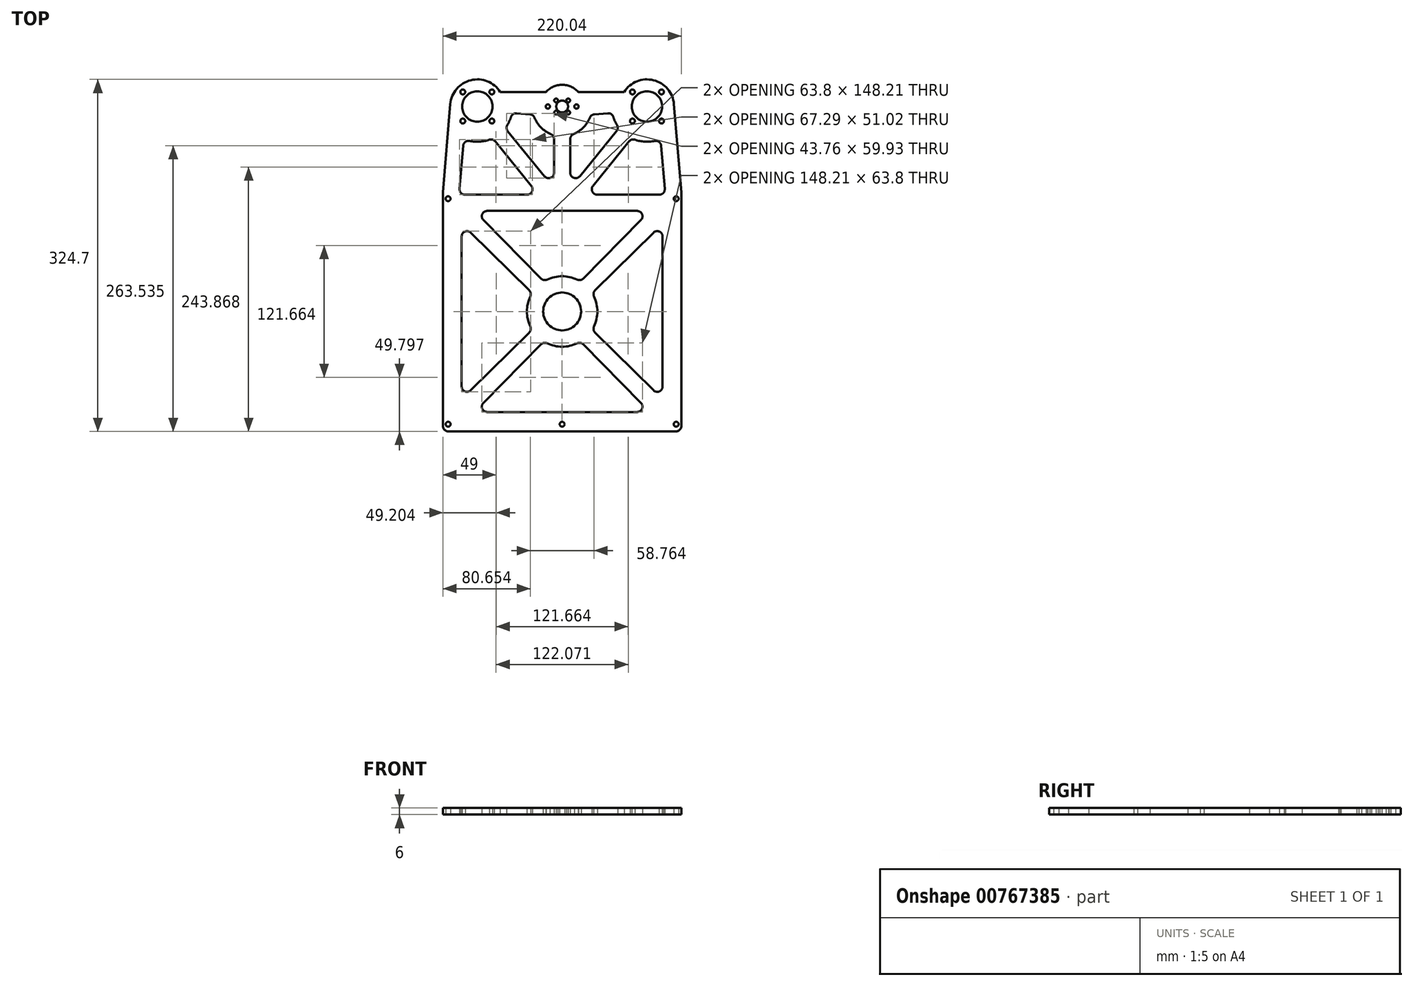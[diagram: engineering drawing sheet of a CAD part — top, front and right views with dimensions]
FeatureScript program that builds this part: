
annotation { "Feature Type Name" : "Feature", "Feature Type Description" : "" }
export const myFeature = defineFeature(function(context is Context, id is Id, definition is map)
    precondition{}
    {
        {
            var Q0;
            Q0=qCreatedBy(makeId("Top.planeOp"),FACE);
            var sketch = newSketch(context, id + "F0", { "sketchPlane" : qUnion([Q0])});
            skLineSegment(sketch, "E0.bottom", {"start": v(129, 146.19) * mm, "end": v(132, 146.19) * mm});
            skLineSegment(sketch, "E1", {"start": v(121.23, -173.81) * mm, "end": v(121.23, 96.42) * mm, "construction": true});
            skPoint(sketch, "E1.endSnap0", {"position": v(16, 96.42) * mm});
            skLineSegment(sketch, "E2", {"start": v(-89.23, -173.81) * mm, "end": v(-89.28, 96.42) * mm, "construction": true});
            skLineSegment(sketch, "E3", {"start": v(-89.28, 96.42) * mm, "end": v(-89.28, 103.45) * mm, "construction": true});
            skLineSegment(sketch, "E4", {"start": v(121.23, 96.42) * mm, "end": v(121.23, 146.19) * mm, "construction": true});
            skCircle(sketch, "E5", {"center": v(-89.27, 41.19) * mm, "radius": 2.25 * mm});
            skCircle(sketch, "E6", {"center": v(-89.23, -166.81) * mm, "radius": 2.25 * mm});
            skCircle(sketch, "E7", {"center": v(121.23, -166.81) * mm, "radius": 2.25 * mm});
            skCircle(sketch, "E8", {"center": v(121.23, 41.19) * mm, "radius": 2.25 * mm});
            skPoint(sketch, "E9.startSnap0", {"position": v(16, -62.81) * mm});
            skLineSegment(sketch, "E10.bottom", {"start": v(-89.04, -173.44) * mm, "end": v(121, -173.44) * mm});
            skLineSegment(sketch, "E10.top", {"start": v(-94.04, 46.77) * mm, "end": v(126, 46.77) * mm, "construction": true});
            skLineSegment(sketch, "E10.left", {"start": v(-94.04, -168.44) * mm, "end": v(-94.04, 46.35) * mm});
            skLineSegment(sketch, "E10.right", {"start": v(126, -168.44) * mm, "end": v(126, 46.36) * mm});
            skLineSegment(sketch, "E11", {"start": v(-89.23, -166.81) * mm, "end": v(121.23, -166.81) * mm, "construction": true});
            skCircle(sketch, "E12", {"center": v(16, -166.81) * mm, "radius": 2.25 * mm});
            skCircle(sketch, "E13", {"center": v(16, 126.26) * mm, "radius": 5.47 * mm});
            skCircle(sketch, "E14", {"center": v(-62.27, 126.26) * mm, "radius": 19 * mm, "construction": true});
            skCircle(sketch, "E15", {"center": v(94.27, 126.26) * mm, "radius": 19 * mm, "construction": true});
            skCircle(sketch, "E16", {"center": v(-62.27, 126.26) * mm, "radius": 14 * mm});
            skCircle(sketch, "E17", {"center": v(94.27, 126.26) * mm, "radius": 14 * mm});
            skCircle(sketch, "E18", {"center": v(-62.27, 126.26) * mm, "radius": 24 * mm, "construction": true});
            skCircle(sketch, "E19", {"center": v(94.27, 126.26) * mm, "radius": 24 * mm, "construction": true});
            skLineSegment(sketch, "E20", {"start": v(-62.27, 126.26) * mm, "end": v(-44.6, 143.94) * mm, "construction": true});
            skCircle(sketch, "E21", {"center": v(-48.84, 139.7) * mm, "radius": 2.25 * mm});
            skCircle(sketch, "E22", {"center": v(-48.84, 139.7) * mm, "radius": 4.25 * mm, "construction": true});
            skCircle(sketch, "E23.1.0", {"center": v(-75.7, 139.7) * mm, "radius": 2.25 * mm});
            skCircle(sketch, "E23.1.1", {"center": v(-75.7, 139.7) * mm, "radius": 4.25 * mm, "construction": true});
            skCircle(sketch, "E23.2.0", {"center": v(-75.7, 112.83) * mm, "radius": 2.25 * mm});
            skCircle(sketch, "E23.2.1", {"center": v(-75.7, 112.83) * mm, "radius": 4.25 * mm, "construction": true});
            skCircle(sketch, "E23.3.0", {"center": v(-48.84, 112.83) * mm, "radius": 2.25 * mm});
            skCircle(sketch, "E23.3.1", {"center": v(-48.84, 112.83) * mm, "radius": 4.25 * mm, "construction": true});
            skLineSegment(sketch, "E24", {"start": v(94.27, 126.26) * mm, "end": v(138.16, 170.16) * mm, "construction": true});
            skCircle(sketch, "E25", {"center": v(107.7, 139.7) * mm, "radius": 2.25 * mm});
            skCircle(sketch, "E26", {"center": v(107.7, 139.7) * mm, "radius": 4.25 * mm, "construction": true});
            skCircle(sketch, "E27.1.0", {"center": v(80.83, 139.7) * mm, "radius": 2.25 * mm});
            skCircle(sketch, "E27.1.1", {"center": v(80.83, 139.7) * mm, "radius": 4.25 * mm, "construction": true});
            skCircle(sketch, "E27.2.0", {"center": v(80.83, 112.83) * mm, "radius": 2.25 * mm});
            skCircle(sketch, "E27.2.1", {"center": v(80.83, 112.83) * mm, "radius": 4.25 * mm, "construction": true});
            skCircle(sketch, "E27.3.0", {"center": v(107.7, 112.83) * mm, "radius": 2.25 * mm});
            skCircle(sketch, "E27.3.1", {"center": v(107.7, 112.83) * mm, "radius": 4.25 * mm, "construction": true});
            skLineSegment(sketch, "E28", {"start": v(21.47, 126.26) * mm, "end": v(36, 126.26) * mm});
            skLineSegment(sketch, "E29", {"start": v(-23.88, -176.81) * mm, "end": v(-3.88, -176.81) * mm});
            skLineSegment(sketch, "E30", {"start": v(35.87, -176.81) * mm, "end": v(55.87, -176.81) * mm});
            skLineSegment(sketch, "E31", {"start": v(-23.9, 41.19) * mm, "end": v(-112.07, 41.19) * mm, "construction": true});
            skLineSegment(sketch, "E32", {"start": v(55.87, 41.19) * mm, "end": v(139.91, 41.19) * mm, "construction": true});
            skLineSegment(sketch, "E33", {"start": v(194.89, 122.83) * mm, "end": v(194.89, 102.83) * mm});
            skLineSegment(sketch, "E34", {"start": v(194.89, 149.7) * mm, "end": v(194.89, 129.7) * mm});
            skCircle(sketch, "E35", {"center": v(16, 126.26) * mm, "radius": 13.2 * mm, "construction": true});
            skCircle(sketch, "E36", {"center": v(16, 126.26) * mm, "radius": 18.25 * mm, "construction": true});
            skCircle(sketch, "E37", {"center": v(29.2, 126.26) * mm, "radius": 2 * mm});
            skArc(sketch, "E38", {"start": v(-41.2, 139.7) * mm, "mid": v(-68.26, 150.54) * mm, "end": v(-87.19, 128.36) * mm});
            skLineSegment(sketch, "E39", {"start": v(-94, 47.2) * mm, "end": v(-87.19, 128.36) * mm});
            skArc(sketch, "E40", {"start": v(36, 126.26) * mm, "mid": v(23.2, 144.92) * mm, "end": v(1.18, 139.7) * mm});
            skLineSegment(sketch, "E41", {"start": v(-41.2, 139.7) * mm, "end": v(1.18, 139.7) * mm});
            skPoint(sketch, "E42.orphan", {"position": v(-84.23, -166.81) * mm});
            skLineSegment(sketch, "E43", {"start": v(-84.23, -161.87) * mm, "end": v(-84.23, 36.25) * mm, "construction": true});
            skArc(sketch, "E44", {"start": v(-1.79, -45.24) * mm, "mid": v(-9, -62.81) * mm, "end": v(-1.79, -80.38) * mm, "construction": true});
            skLineSegment(sketch, "E45.trimOffspring", {"start": v(-84.23, 36.25) * mm, "end": v(-1.79, -45.24) * mm, "construction": true});
            skLineSegment(sketch, "E46.trimOffspring", {"start": v(119.63, 39.6) * mm, "end": v(121.23, 41.19) * mm, "construction": true});
            skLineSegment(sketch, "E47.trimOffspring", {"start": v(119.63, -165.23) * mm, "end": v(121.23, -166.81) * mm, "construction": true});
            skLineSegment(sketch, "E48.trimOffspring", {"start": v(-84.23, -161.87) * mm, "end": v(-1.79, -80.38) * mm, "construction": true});
            skLineSegment(sketch, "E49.0", {"start": v(-68.22, 9.88) * mm, "end": v(-14.42, -43.3) * mm});
            skLineSegment(sketch, "E49.1", {"start": v(-76.73, -131.94) * mm, "end": v(-76.73, 6.32) * mm});
            skLineSegment(sketch, "E49.2", {"start": v(-68.22, -135.5) * mm, "end": v(-14.42, -82.33) * mm});
            skArc(sketch, "E49.3", {"start": v(-13.41, -48.98) * mm, "mid": v(-16.5, -62.81) * mm, "end": v(-13.41, -76.64) * mm});
            skPoint(sketch, "E50.visualSharp", {"position": v(-76.73, 18.3) * mm});
            skArc(sketch, "E50.filletArc", {"start": v(-68.22, 9.88) * mm, "mid": v(-73.66, 10.93) * mm, "end": v(-76.73, 6.32) * mm});
            skPoint(sketch, "E51.visualSharp", {"position": v(-76.73, -143.91) * mm});
            skArc(sketch, "E51.filletArc", {"start": v(-76.73, -131.94) * mm, "mid": v(-73.66, -136.55) * mm, "end": v(-68.22, -135.5) * mm});
            skPoint(sketch, "E52.visualSharp", {"position": v(-11.77, -79.7) * mm});
            skArc(sketch, "E52.filletArc", {"start": v(-14.42, -82.33) * mm, "mid": v(-13.01, -79.65) * mm, "end": v(-13.41, -76.64) * mm});
            skPoint(sketch, "E53.visualSharp", {"position": v(-11.77, -45.92) * mm});
            skArc(sketch, "E53.filletArc", {"start": v(-13.41, -48.98) * mm, "mid": v(-13.01, -45.97) * mm, "end": v(-14.42, -43.3) * mm});
            skPoint(sketch, "E54.visualSharp", {"position": v(-94.04, 46.77) * mm});
            skArc(sketch, "E54.filletArc", {"start": v(-94, 47.2) * mm, "mid": v(-94.03, 46.77) * mm, "end": v(-94.04, 46.35) * mm});
            skPoint(sketch, "E55.visualSharp", {"position": v(-94.04, -173.44) * mm});
            skArc(sketch, "E55.filletArc", {"start": v(-94.04, -168.44) * mm, "mid": v(-92.57, -171.97) * mm, "end": v(-89.04, -173.44) * mm});
            skCircle(sketch, "E56", {"center": v(94.27, 126.26) * mm, "radius": 25 * mm});
            skLineSegment(sketch, "E57", {"start": v(30.81, 139.7) * mm, "end": v(73.18, 139.7) * mm});
            skLineSegment(sketch, "E58", {"start": v(125.96, 47.19) * mm, "end": v(119.18, 128.34) * mm});
            skPoint(sketch, "E59.visualSharp", {"position": v(126, 46.77) * mm});
            skArc(sketch, "E59.filletArc", {"start": v(126, 46.36) * mm, "mid": v(125.99, 46.77) * mm, "end": v(125.96, 47.19) * mm});
            skPoint(sketch, "E60.visualSharp", {"position": v(126, -173.44) * mm});
            skArc(sketch, "E60.filletArc", {"start": v(121, -173.44) * mm, "mid": v(124.53, -171.97) * mm, "end": v(126, -168.44) * mm});
            skArc(sketch, "E61.1.0", {"start": v(35.51, -93.23) * mm, "mid": v(32.83, -91.82) * mm, "end": v(29.83, -92.22) * mm});
            skArc(sketch, "E61.1.1", {"start": v(2.16, -92.22) * mm, "mid": v(16, -95.31) * mm, "end": v(29.83, -92.22) * mm});
            skLineSegment(sketch, "E61.1.2", {"start": v(88.68, -147.03) * mm, "end": v(35.51, -93.23) * mm});
            skArc(sketch, "E61.1.3", {"start": v(85.13, -155.54) * mm, "mid": v(89.74, -152.47) * mm, "end": v(88.68, -147.03) * mm});
            skLineSegment(sketch, "E61.1.4", {"start": v(85.13, -155.54) * mm, "end": v(-53.13, -155.54) * mm});
            skArc(sketch, "E61.1.5", {"start": v(-56.7, -147.03) * mm, "mid": v(-57.75, -152.47) * mm, "end": v(-53.13, -155.54) * mm});
            skLineSegment(sketch, "E61.1.6", {"start": v(-56.7, -147.03) * mm, "end": v(-3.52, -93.23) * mm});
            skArc(sketch, "E61.1.7", {"start": v(2.16, -92.22) * mm, "mid": v(-0.84, -91.82) * mm, "end": v(-3.52, -93.23) * mm});
            skArc(sketch, "E61.2.0", {"start": v(46.41, -43.3) * mm, "mid": v(45, -45.97) * mm, "end": v(45.4, -48.98) * mm});
            skArc(sketch, "E61.2.1", {"start": v(45.4, -76.64) * mm, "mid": v(48.5, -62.81) * mm, "end": v(45.4, -48.98) * mm});
            skLineSegment(sketch, "E61.2.2", {"start": v(100.21, 9.88) * mm, "end": v(46.41, -43.3) * mm});
            skArc(sketch, "E61.2.3", {"start": v(108.73, 6.32) * mm, "mid": v(105.65, 10.93) * mm, "end": v(100.21, 9.88) * mm});
            skLineSegment(sketch, "E61.2.4", {"start": v(108.73, 6.32) * mm, "end": v(108.73, -131.94) * mm});
            skArc(sketch, "E61.2.5", {"start": v(100.21, -135.5) * mm, "mid": v(105.65, -136.55) * mm, "end": v(108.73, -131.94) * mm});
            skLineSegment(sketch, "E61.2.6", {"start": v(100.21, -135.5) * mm, "end": v(46.41, -82.33) * mm});
            skArc(sketch, "E61.2.7", {"start": v(45.4, -76.64) * mm, "mid": v(45, -79.65) * mm, "end": v(46.41, -82.33) * mm});
            skArc(sketch, "E61.3.0", {"start": v(-3.52, -32.4) * mm, "mid": v(-0.84, -33.8) * mm, "end": v(2.16, -33.4) * mm});
            skArc(sketch, "E61.3.1", {"start": v(29.83, -33.4) * mm, "mid": v(16, -30.31) * mm, "end": v(2.16, -33.4) * mm});
            skLineSegment(sketch, "E61.3.2", {"start": v(-56.7, 21.4) * mm, "end": v(-3.52, -32.4) * mm});
            skArc(sketch, "E61.3.3", {"start": v(-53.13, 29.92) * mm, "mid": v(-57.75, 26.85) * mm, "end": v(-56.7, 21.4) * mm});
            skLineSegment(sketch, "E61.3.4", {"start": v(-53.13, 29.92) * mm, "end": v(85.13, 29.92) * mm});
            skArc(sketch, "E61.3.5", {"start": v(88.68, 21.4) * mm, "mid": v(89.74, 26.85) * mm, "end": v(85.13, 29.92) * mm});
            skLineSegment(sketch, "E61.3.6", {"start": v(88.68, 21.4) * mm, "end": v(35.51, -32.4) * mm});
            skArc(sketch, "E61.3.7", {"start": v(29.83, -33.4) * mm, "mid": v(32.83, -33.8) * mm, "end": v(35.51, -32.4) * mm});
            skLineSegment(sketch, "E62", {"start": v(16, 126.26) * mm, "end": v(16, 108.01) * mm, "construction": true});
            skLineSegment(sketch, "E63", {"start": v(16, 29.92) * mm, "end": v(-46.51, 106.86) * mm, "construction": true});
            skLineSegment(sketch, "E64", {"start": v(94.27, 126.26) * mm, "end": v(78.5, 106.86) * mm, "construction": true});
            skLineSegment(sketch, "E65.trimOffspring", {"start": v(-62.27, 126.26) * mm, "end": v(132, 126.26) * mm, "construction": true});
            skLineSegment(sketch, "E66.trimOffspring", {"start": v(69.27, 126.26) * mm, "end": v(70.27, 126.26) * mm});
            skArc(sketch, "E67.trimOffspring", {"start": v(-4, 125.75) * mm, "mid": v(2.04, 111.94) * mm, "end": v(16, 106.26) * mm, "construction": true});
            skArc(sketch, "E68.trimOffspring", {"start": v(-46.51, 106.86) * mm, "mid": v(-39.24, 116.55) * mm, "end": v(-37.38, 128.52) * mm, "construction": true});
            skLineSegment(sketch, "E69.trimOffspring", {"start": v(16, 106.26) * mm, "end": v(16, -252.1) * mm, "construction": true});
            skLineSegment(sketch, "E70.trimOffspring", {"start": v(-47.14, 107.64) * mm, "end": v(-62.27, 126.26) * mm, "construction": true});
            skLineSegment(sketch, "E71", {"start": v(16, 106.26) * mm, "end": v(16, 29.92) * mm, "construction": true});
            skLineSegment(sketch, "E72.0", {"start": v(-0.38, 61.98) * mm, "end": v(-34.16, 103.55) * mm});
            skLineSegment(sketch, "E72.1", {"start": v(8.5, 96.26) * mm, "end": v(8.5, 65.13) * mm});
            skLineSegment(sketch, "E72.3", {"start": v(-26.07, 120.06) * mm, "end": v(-13.7, 119.03) * mm});
            skArc(sketch, "E72.4", {"start": v(-9.49, 115.93) * mm, "mid": v(-3.54, 106.91) * mm, "end": v(5.42, 100.88) * mm});
            skPoint(sketch, "E73.visualSharp", {"position": v(8.5, 51.05) * mm});
            skArc(sketch, "E73.filletArc", {"start": v(-0.38, 61.98) * mm, "mid": v(5.17, 60.42) * mm, "end": v(8.5, 65.13) * mm});
            skPoint(sketch, "E74.visualSharp", {"position": v(-36.51, 106.45) * mm});
            skArc(sketch, "E74.filletArc", {"start": v(-34.55, 109.31) * mm, "mid": v(-35.27, 106.37) * mm, "end": v(-34.16, 103.55) * mm});
            skPoint(sketch, "E75.visualSharp", {"position": v(-30.3, 120.4) * mm});
            skArc(sketch, "E75.filletArc", {"start": v(-26.07, 120.06) * mm, "mid": v(-29.27, 119.22) * mm, "end": v(-31.25, 116.57) * mm});
            skPoint(sketch, "E76.visualSharp", {"position": v(-10.46, 118.76) * mm});
            skArc(sketch, "E76.filletArc", {"start": v(-9.49, 115.93) * mm, "mid": v(-11.16, 118.08) * mm, "end": v(-13.7, 119.03) * mm});
            skPoint(sketch, "E77.visualSharp", {"position": v(8.5, 99.8) * mm});
            skArc(sketch, "E77.filletArc", {"start": v(8.5, 96.26) * mm, "mid": v(7.66, 99.04) * mm, "end": v(5.42, 100.88) * mm});
            skLineSegment(sketch, "E78.MirrorCS", {"start": v(-12.48, 53.07) * mm, "end": v(-45.8, 94.1) * mm});
            skPoint(sketch, "E79.MirrorP", {"position": v(-48.16, 96.99) * mm});
            skArc(sketch, "E80.MirrorCS", {"start": v(-51.36, 95.65) * mm, "mid": v(-48.33, 95.75) * mm, "end": v(-45.8, 94.1) * mm});
            skArc(sketch, "E81", {"start": v(-34.55, 109.31) * mm, "mid": v(-32.68, 112.84) * mm, "end": v(-31.25, 116.57) * mm});
            skArc(sketch, "E82.trimOffspring", {"start": v(-69.29, 94.53) * mm, "mid": v(-60.25, 93.83) * mm, "end": v(-51.36, 95.65) * mm});
            skPoint(sketch, "E83.trimOffspring.end.orphan", {"position": v(-89.28, 146.19) * mm});
            skLineSegment(sketch, "E84.0", {"start": v(-78.69, 50.34) * mm, "end": v(-75.35, 90.07) * mm});
            skLineSegment(sketch, "E85.0", {"start": v(-73.7, 44.92) * mm, "end": v(-16.36, 44.92) * mm});
            skPoint(sketch, "E86.visualSharp", {"position": v(-74.83, 96.29) * mm});
            skArc(sketch, "E86.filletArc", {"start": v(-69.29, 94.53) * mm, "mid": v(-73.33, 93.67) * mm, "end": v(-75.35, 90.07) * mm});
            skPoint(sketch, "E87.visualSharp", {"position": v(-79.14, 44.92) * mm});
            skArc(sketch, "E87.filletArc", {"start": v(-78.69, 50.34) * mm, "mid": v(-77.38, 46.53) * mm, "end": v(-73.7, 44.92) * mm});
            skPoint(sketch, "E88.visualSharp", {"position": v(-5.85, 44.92) * mm});
            skArc(sketch, "E88.filletArc", {"start": v(-16.36, 44.92) * mm, "mid": v(-11.84, 47.77) * mm, "end": v(-12.48, 53.07) * mm});
            skCircle(sketch, "E89", {"center": v(2.8, 126.26) * mm, "radius": 2 * mm});
            skCircle(sketch, "E90", {"center": v(16, 126.26) * mm, "radius": 7.92 * mm, "construction": true});
            skLineSegment(sketch, "E91", {"start": v(16, 126.26) * mm, "end": v(38.6, 148.88) * mm, "construction": true});
            skCircle(sketch, "E92", {"center": v(21.6, 131.86) * mm, "radius": 1.75 * mm});
            skCircle(sketch, "E93.1.0", {"center": v(10.4, 131.86) * mm, "radius": 1.75 * mm});
            skCircle(sketch, "E93.2.0", {"center": v(10.4, 120.67) * mm, "radius": 1.75 * mm});
            skCircle(sketch, "E93.3.0", {"center": v(21.6, 120.67) * mm, "radius": 1.75 * mm});
            skArc(sketch, "E94.MirrorCS", {"start": v(23.5, 96.26) * mm, "mid": v(24.34, 99.04) * mm, "end": v(26.57, 100.88) * mm});
            skArc(sketch, "E95.MirrorCS", {"start": v(41.48, 115.93) * mm, "mid": v(35.53, 106.91) * mm, "end": v(26.57, 100.88) * mm});
            skPoint(sketch, "E96.MirrorP", {"position": v(23.5, 99.8) * mm});
            skLineSegment(sketch, "E97.MirrorCS", {"start": v(16, 29.92) * mm, "end": v(78.5, 106.86) * mm, "construction": true});
            skArc(sketch, "E98.MirrorCS", {"start": v(32.38, 61.98) * mm, "mid": v(26.82, 60.42) * mm, "end": v(23.5, 65.13) * mm});
            skLineSegment(sketch, "E99.MirrorCS", {"start": v(32.38, 61.98) * mm, "end": v(66.15, 103.55) * mm});
            skLineSegment(sketch, "E100.MirrorCS", {"start": v(44.47, 53.07) * mm, "end": v(77.8, 94.1) * mm});
            skLineSegment(sketch, "E101.MirrorCS", {"start": v(23.5, 96.26) * mm, "end": v(23.5, 65.13) * mm});
            skArc(sketch, "E102.MirrorCS", {"start": v(41.48, 115.93) * mm, "mid": v(43.15, 118.08) * mm, "end": v(45.7, 119.03) * mm});
            skLineSegment(sketch, "E103.MirrorCS", {"start": v(58.06, 120.06) * mm, "end": v(45.7, 119.03) * mm});
            skArc(sketch, "E104.MirrorCS", {"start": v(58.06, 120.06) * mm, "mid": v(61.27, 119.22) * mm, "end": v(63.25, 116.57) * mm});
            skArc(sketch, "E105.MirrorCS", {"start": v(66.54, 109.31) * mm, "mid": v(64.67, 112.84) * mm, "end": v(63.25, 116.57) * mm});
            skArc(sketch, "E106.MirrorCS", {"start": v(66.54, 109.31) * mm, "mid": v(67.26, 106.37) * mm, "end": v(66.15, 103.55) * mm});
            skArc(sketch, "E107.MirrorCS", {"start": v(83.35, 95.65) * mm, "mid": v(80.33, 95.75) * mm, "end": v(77.8, 94.1) * mm});
            skArc(sketch, "E108.MirrorCS", {"start": v(101.28, 94.53) * mm, "mid": v(92.24, 93.83) * mm, "end": v(83.35, 95.65) * mm});
            skArc(sketch, "E109.MirrorCS", {"start": v(101.28, 94.53) * mm, "mid": v(105.32, 93.67) * mm, "end": v(107.34, 90.07) * mm});
            skLineSegment(sketch, "E110.MirrorCS", {"start": v(110.68, 50.34) * mm, "end": v(107.34, 90.07) * mm});
            skArc(sketch, "E111.MirrorCS", {"start": v(110.68, 50.34) * mm, "mid": v(109.38, 46.53) * mm, "end": v(105.7, 44.92) * mm});
            skLineSegment(sketch, "E112.MirrorCS", {"start": v(105.7, 44.92) * mm, "end": v(48.35, 44.92) * mm});
            skArc(sketch, "E113.MirrorCS", {"start": v(48.35, 44.92) * mm, "mid": v(43.83, 47.77) * mm, "end": v(44.47, 53.07) * mm});
            skCircle(sketch, "E114", {"center": v(16, -62.81) * mm, "radius": 17.5 * mm});
            skSolve(sketch);
        }
        {
            var Q0;
            Q0=makeQuery(id+"F0.imprint","IMPRINT",FACE,{"disambiguationData":[TD([[makeQuery(id+"F0.imprint","IMPRINT",EDGE,{"derivedFrom":sQuery(id+"F0.wireOp",EDGE,"E5")}),-1.0]])]});
            var Q1;
            Q1=makeQuery(id+"F0.imprint","IMPRINT",FACE,{"disambiguationData":[TD([[makeQuery(id+"F0.imprint","IMPRINT",EDGE,{"derivedFrom":sQuery(id+"F0.wireOp",EDGE,"E17")}),-1.0]])]});
            extrude(context, id + "F1", {"entities" : qUnion([Q0, Q1]), "depth" : 6 * mm, "offsetDistance" : 25 * mm});
        }
    });
